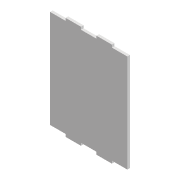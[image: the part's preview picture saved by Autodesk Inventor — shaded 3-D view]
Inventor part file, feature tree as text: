
AUTODESK INVENTOR PART (.ipt)
format: ipt  version: 2022 (Build 260153000, 153)  size: 98,304 bytes
history: native  units: mm
features: reference x3, other x3, extrude x1, sketch x1
ambient origin geometry x8: Origin, YZ Plane, XZ Plane, XY Plane, X Axis, Y Axis, Z Axis, Center Point
bodies: Solid1 (feature_tree)
feature tree (8):
  extrude  "Extrusion1"  Depth=5.0mm
  sketch  "Sketch1"  dims[d0=30.0mm d1=5.0mm d2=30.0mm d3=5.0mm d4=5.0mm d5=0.0mm]
  reference  "Reference1"
  reference  "Reference2"
  reference  "Reference3"
  other  "Assembly2"
  other  "Modelo base:1"
  other  "Frontal:1"
